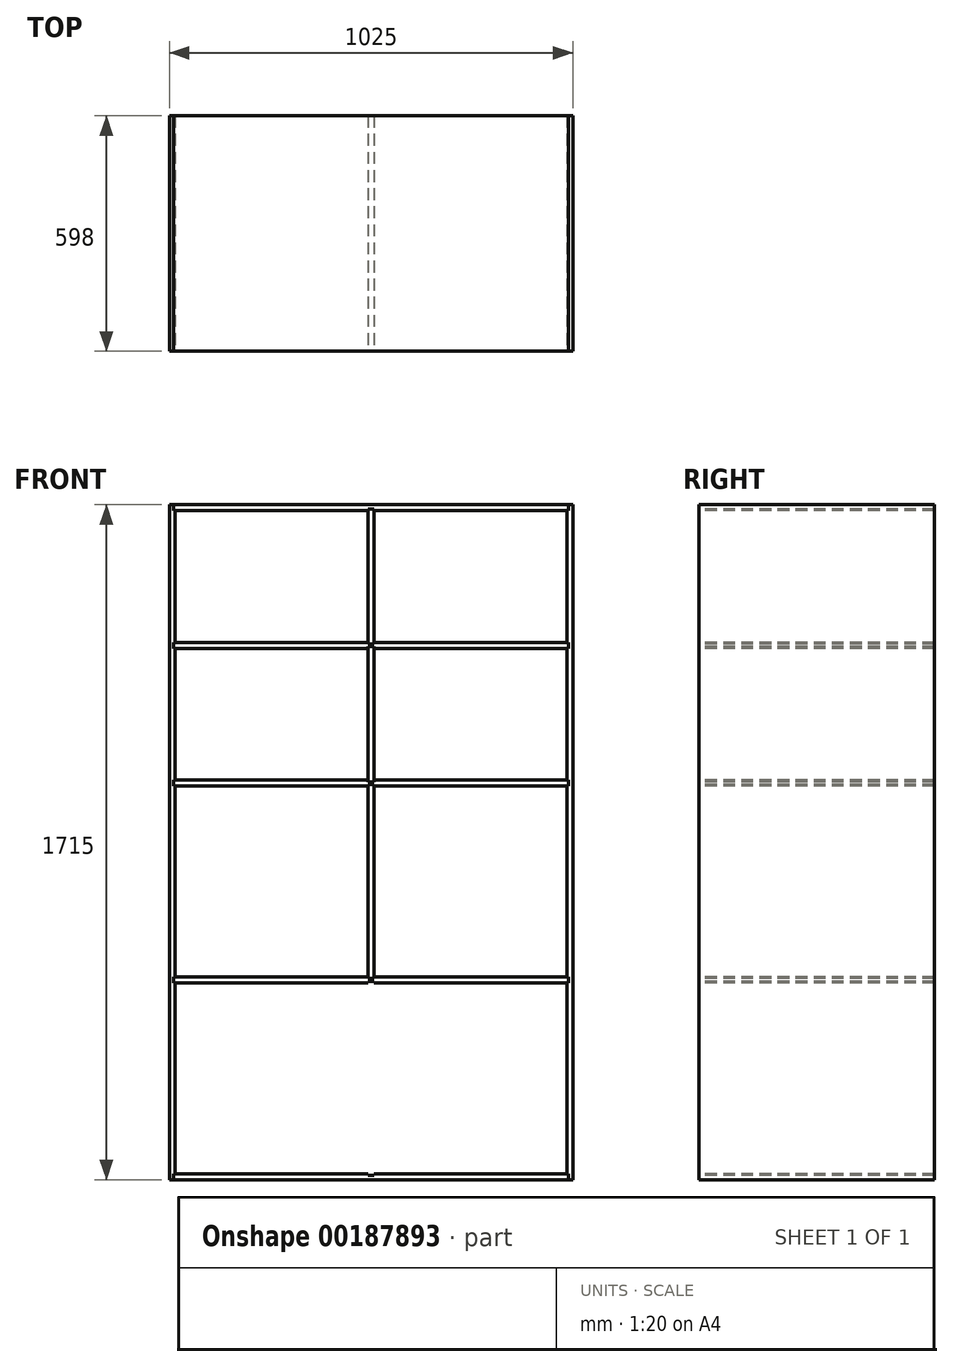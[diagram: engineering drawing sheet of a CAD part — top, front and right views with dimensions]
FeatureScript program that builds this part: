
annotation { "Feature Type Name" : "Feature", "Feature Type Description" : "" }
export const myFeature = defineFeature(function(context is Context, id is Id, definition is map)
    precondition{}
    {
        {
            assignVariable(context, id + "F0", {"name" : "depth", "anyValue" : 598});
        }
        {
            var Q0;
            Q0=qCreatedBy(makeId("Front.planeOp"),FACE);
            var sketch = newSketch(context, id + "F1", { "sketchPlane" : qUnion([Q0])});
            skLineSegment(sketch, "E0.bottom", {"start": v(497.5, 842.5) * mm, "end": v(7.5, 842.5) * mm});
            skLineSegment(sketch, "E0.top", {"start": v(497.5, -842.5) * mm, "end": v(7.5, -842.5) * mm});
            skLineSegment(sketch, "E0.left", {"start": v(497.5, 842.5) * mm, "end": v(497.5, 507.5) * mm});
            skLineSegment(sketch, "E0.right", {"start": v(-497.5, 842.5) * mm, "end": v(-497.5, 507.5) * mm});
            skPoint(sketch, "E0.middle", {"position": v(0, 0) * mm});
            skLineSegment(sketch, "E1.0", {"start": v(512.5, 857.5) * mm, "end": v(-512.5, 857.5) * mm});
            skLineSegment(sketch, "E1.1", {"start": v(512.5, 857.5) * mm, "end": v(512.5, -857.5) * mm});
            skLineSegment(sketch, "E1.2", {"start": v(512.5, -857.5) * mm, "end": v(-512.5, -857.5) * mm});
            skLineSegment(sketch, "E1.3", {"start": v(-512.5, 857.5) * mm, "end": v(-512.5, -857.5) * mm});
            skLineSegment(sketch, "E2", {"start": v(-501.5, 857.5) * mm, "end": v(-501.5, 842.5) * mm});
            skLineSegment(sketch, "E3", {"start": v(-501.5, 842.5) * mm, "end": v(-497.5, 842.5) * mm});
            skLineSegment(sketch, "E4", {"start": v(497.5, 842.5) * mm, "end": v(501.5, 842.5) * mm});
            skLineSegment(sketch, "E5", {"start": v(501.5, 842.5) * mm, "end": v(501.5, 857.5) * mm});
            skLineSegment(sketch, "E6", {"start": v(0, 0) * mm, "end": v(-733.8, 0) * mm, "construction": true});
            skPoint(sketch, "E6.endSnap0", {"position": v(-497.5, 0) * mm});
            skLineSegment(sketch, "E7.MirrorCS", {"start": v(501.5, -842.5) * mm, "end": v(501.5, -857.5) * mm});
            skLineSegment(sketch, "E8.MirrorCS", {"start": v(497.5, -842.5) * mm, "end": v(501.5, -842.5) * mm});
            skLineSegment(sketch, "E9.MirrorCS", {"start": v(-501.5, -857.5) * mm, "end": v(-501.5, -842.5) * mm});
            skLineSegment(sketch, "E10.MirrorCS", {"start": v(-501.5, -842.5) * mm, "end": v(-497.5, -842.5) * mm});
            skLineSegment(sketch, "E11.bottom", {"start": v(-501.5, 507.5) * mm, "end": v(-7.5, 507.5) * mm});
            skLineSegment(sketch, "E11.top", {"start": v(-501.5, 492.5) * mm, "end": v(-7.5, 492.5) * mm});
            skLineSegment(sketch, "E11.left", {"start": v(-501.5, 507.5) * mm, "end": v(-501.5, 492.5) * mm});
            skLineSegment(sketch, "E11.right", {"start": v(501.5, 507.5) * mm, "end": v(501.5, 492.5) * mm});
            skLineSegment(sketch, "E12.bottom", {"start": v(-501.5, -342.5) * mm, "end": v(-7.5, -342.5) * mm});
            skLineSegment(sketch, "E12.top", {"start": v(-501.5, -357.5) * mm, "end": v(-7.5, -357.5) * mm});
            skLineSegment(sketch, "E12.left", {"start": v(-501.5, -342.5) * mm, "end": v(-501.5, -357.5) * mm});
            skLineSegment(sketch, "E12.right", {"start": v(501.5, -342.5) * mm, "end": v(501.5, -357.5) * mm});
            skLineSegment(sketch, "E13.bottom", {"start": v(-501.5, 157.5) * mm, "end": v(-7.5, 157.5) * mm});
            skLineSegment(sketch, "E13.top", {"start": v(-501.5, 142.5) * mm, "end": v(-7.5, 142.5) * mm});
            skLineSegment(sketch, "E13.left", {"start": v(-501.5, 157.5) * mm, "end": v(-501.5, 142.5) * mm});
            skLineSegment(sketch, "E13.right", {"start": v(501.5, 157.5) * mm, "end": v(501.5, 142.5) * mm});
            skLineSegment(sketch, "E14.trimOffspring", {"start": v(-497.5, 492.5) * mm, "end": v(-497.5, 157.5) * mm});
            skLineSegment(sketch, "E15.trimOffspring", {"start": v(-497.5, 142.5) * mm, "end": v(-497.5, -342.5) * mm});
            skLineSegment(sketch, "E16.trimOffspring", {"start": v(-497.5, -357.5) * mm, "end": v(-497.5, -842.5) * mm});
            skLineSegment(sketch, "E17.trimOffspring", {"start": v(497.5, 492.5) * mm, "end": v(497.5, 157.5) * mm});
            skLineSegment(sketch, "E18.trimOffspring", {"start": v(497.5, 142.5) * mm, "end": v(497.5, -342.5) * mm});
            skLineSegment(sketch, "E19.trimOffspring", {"start": v(497.5, -357.5) * mm, "end": v(497.5, -842.5) * mm});
            skLineSegment(sketch, "E20.bottom", {"start": v(-7.5, 846.5) * mm, "end": v(7.5, 846.5) * mm});
            skLineSegment(sketch, "E20.top", {"start": v(-7.5, 503.5) * mm, "end": v(7.5, 503.5) * mm});
            skLineSegment(sketch, "E20.left", {"start": v(-7.5, 846.5) * mm, "end": v(-7.5, 503.5) * mm});
            skLineSegment(sketch, "E20.right", {"start": v(7.5, 846.5) * mm, "end": v(7.5, 503.5) * mm});
            skLineSegment(sketch, "E21", {"start": v(0, 0) * mm, "end": v(0, 1057.18) * mm, "construction": true});
            skLineSegment(sketch, "E22.trimOffspring", {"start": v(-7.5, 842.5) * mm, "end": v(-497.5, 842.5) * mm});
            skLineSegment(sketch, "E23.trimOffspring", {"start": v(7.5, 507.5) * mm, "end": v(501.5, 507.5) * mm});
            skLineSegment(sketch, "E24.bottom", {"start": v(-7.5, 496.5) * mm, "end": v(7.5, 496.5) * mm});
            skLineSegment(sketch, "E24.top", {"start": v(-7.5, 153.5) * mm, "end": v(7.5, 153.5) * mm});
            skLineSegment(sketch, "E24.left", {"start": v(-7.5, 496.5) * mm, "end": v(-7.5, 153.5) * mm});
            skLineSegment(sketch, "E24.right", {"start": v(7.5, 496.5) * mm, "end": v(7.5, 153.5) * mm});
            skLineSegment(sketch, "E25.trimOffspring", {"start": v(7.5, 492.5) * mm, "end": v(501.5, 492.5) * mm});
            skLineSegment(sketch, "E26.trimOffspring", {"start": v(7.5, 157.5) * mm, "end": v(501.5, 157.5) * mm});
            skLineSegment(sketch, "E27.MirrorCS", {"start": v(-7.5, -846.5) * mm, "end": v(7.5, -846.5) * mm});
            skLineSegment(sketch, "E28.trimOffspring", {"start": v(7.5, 142.5) * mm, "end": v(501.5, 142.5) * mm});
            skLineSegment(sketch, "E29.trimOffspring", {"start": v(7.5, -342.5) * mm, "end": v(501.5, -342.5) * mm});
            skLineSegment(sketch, "E30.trimOffspring", {"start": v(7.5, -357.5) * mm, "end": v(501.5, -357.5) * mm});
            skLineSegment(sketch, "E31.trimOffspring", {"start": v(-7.5, -842.5) * mm, "end": v(-497.5, -842.5) * mm});
            skLineSegment(sketch, "E32.bottom", {"start": v(-7.5, 146.5) * mm, "end": v(7.5, 146.5) * mm});
            skLineSegment(sketch, "E32.top", {"start": v(-7.5, -346.5) * mm, "end": v(7.5, -346.5) * mm});
            skLineSegment(sketch, "E32.left", {"start": v(-7.5, 146.5) * mm, "end": v(-7.5, -346.5) * mm});
            skLineSegment(sketch, "E32.right", {"start": v(7.5, 146.5) * mm, "end": v(7.5, -346.5) * mm});
            skLineSegment(sketch, "E33.bottom", {"start": v(7.5, -846.5) * mm, "end": v(-7.5, -846.5) * mm});
            skLineSegment(sketch, "E33.top", {"start": v(7.5, -353.5) * mm, "end": v(-7.5, -353.5) * mm});
            skLineSegment(sketch, "E33.left", {"start": v(7.5, -846.5) * mm, "end": v(7.5, -353.5) * mm});
            skLineSegment(sketch, "E33.right", {"start": v(-7.5, -846.5) * mm, "end": v(-7.5, -353.5) * mm});
            skSolve(sketch);
        }
        {
            var Q0;
            {var subQ4=sQuery(id+"F1.wireOp",EDGE,"E0.right");Q0=makeQuery(id+"F1.imprint","IMPRINT",FACE,{"disambiguationData":[TD([[makeQuery(id+"F1.imprint","IMPRINT",EDGE,{"derivedFrom":subQ4}),-1.0]])]});}
            extrude(context, id + "F2", {"entities" : qUnion([Q0]), "oppositeDirection" : true, "depth" : (getVariable(context, 'depth')) * mm});
        }
        {
            var Q0;
            {var subQ6=sQuery(id+"F1.wireOp",EDGE,"E0.left");Q0=makeQuery(id+"F1.imprint","IMPRINT",FACE,{"disambiguationData":[TD([[makeQuery(id+"F1.imprint","IMPRINT",EDGE,{"derivedFrom":subQ6}),1.0]])]});}
            extrude(context, id + "F3", {"entities" : qUnion([Q0]), "oppositeDirection" : true, "depth" : (getVariable(context, 'depth')) * mm});
        }
        {
            var Q0;
            {var subQ4=sQuery(id+"F1.wireOp",EDGE,"E0.bottom");Q0=makeQuery(id+"F1.imprint","IMPRINT",FACE,{"disambiguationData":[TD([[makeQuery(id+"F1.imprint","IMPRINT",EDGE,{"derivedFrom":subQ4}),-1.0]])]});}
            var Q1;
            {var subQ4=sQuery(id+"F1.wireOp",EDGE,"E0.top");Q1=makeQuery(id+"F1.imprint","IMPRINT",FACE,{"disambiguationData":[TD([[makeQuery(id+"F1.imprint","IMPRINT",EDGE,{"derivedFrom":subQ4}),1.0]])]});}
            extrude(context, id + "F4", {"entities" : qUnion([Q0, Q1]), "oppositeDirection" : true, "depth" : (getVariable(context, 'depth')) * mm});
        }
        {
            var Q0;
            {var subQ10=sQuery(id+"F1.wireOp",EDGE,"E12.left");Q0=makeQuery(id+"F1.imprint","IMPRINT",FACE,{"disambiguationData":[TD([[makeQuery(id+"F1.imprint","IMPRINT",EDGE,{"derivedFrom":subQ10}),1.0]])]});}
            extrude(context, id + "F5", {"entities" : qUnion([Q0]), "oppositeDirection" : true, "depth" : (getVariable(context, 'depth')) * mm});
        }
        {
            var Q0;
            {var subQ3=sQuery(id+"F1.wireOp",EDGE,"E20.bottom");Q0=makeQuery(id+"F1.imprint","IMPRINT",FACE,{"disambiguationData":[TD([[makeQuery(id+"F1.imprint","IMPRINT",EDGE,{"derivedFrom":subQ3}),-1.0]])]});}
            var Q1;
            {var subQ3=sQuery(id+"F1.wireOp",EDGE,"E24.bottom");Q1=makeQuery(id+"F1.imprint","IMPRINT",FACE,{"disambiguationData":[TD([[makeQuery(id+"F1.imprint","IMPRINT",EDGE,{"derivedFrom":subQ3}),-1.0]])]});}
            var Q2;
            {var subQ3=sQuery(id+"F1.wireOp",EDGE,"b123904b-0ea1-4822-b1ab-146c09b0633c0.MirrorCS");Q2=makeQuery(id+"F1.imprint","IMPRINT",FACE,{"disambiguationData":[TD([[makeQuery(id+"F1.imprint","IMPRINT",EDGE,{"derivedFrom":subQ3}),1.0]])]});}
            var Q3;
            {var subQ6=sQuery(id+"F1.wireOp",EDGE,"b123904b-0ea1-4822-b1ab-146c09b0633c1.MirrorCS");Q3=makeQuery(id+"F1.imprint","IMPRINT",FACE,{"disambiguationData":[TD([[makeQuery(id+"F1.imprint","IMPRINT",EDGE,{"derivedFrom":subQ6}),-1.0]])]});}
            extrude(context, id + "F6", {"entities" : qUnion([Q0, Q1, Q2, Q3]), "oppositeDirection" : true, "depth" : (getVariable(context, 'depth')) * mm});
        }
        {
            var Q0;
            {var subQ3=sQuery(id+"F1.wireOp",EDGE,"E33.bottom");Q0=makeQuery(id+"F1.imprint","IMPRINT",FACE,{"disambiguationData":[TD([[makeQuery(id+"F1.imprint","IMPRINT",EDGE,{"derivedFrom":subQ3}),-1.0]])]});}
            var Q1;
            {var subQ3=sQuery(id+"F1.wireOp",EDGE,"E32.bottom");Q1=makeQuery(id+"F1.imprint","IMPRINT",FACE,{"disambiguationData":[TD([[makeQuery(id+"F1.imprint","IMPRINT",EDGE,{"derivedFrom":subQ3}),-1.0]])]});}
            extrude(context, id + "F7", {"entities" : qUnion([Q0, Q1]), "oppositeDirection" : true, "depth" : 598 * mm});
        }
        {
            var Q0;
            {var subQ12=sQuery(id+"F1.wireOp",EDGE,"E11.left");Q0=makeQuery(id+"F1.imprint","IMPRINT",FACE,{"disambiguationData":[TD([[makeQuery(id+"F1.imprint","IMPRINT",EDGE,{"derivedFrom":subQ12}),1.0]])]});}
            var Q1;
            {var subQ5=sQuery(id+"F1.wireOp",EDGE,"E13.left");Q1=makeQuery(id+"F1.imprint","IMPRINT",FACE,{"disambiguationData":[TD([[makeQuery(id+"F1.imprint","IMPRINT",EDGE,{"derivedFrom":subQ5}),1.0]])]});}
            extrude(context, id + "F8", {"entities" : qUnion([Q0, Q1]), "oppositeDirection" : true, "depth" : 598 * mm});
        }
    });
